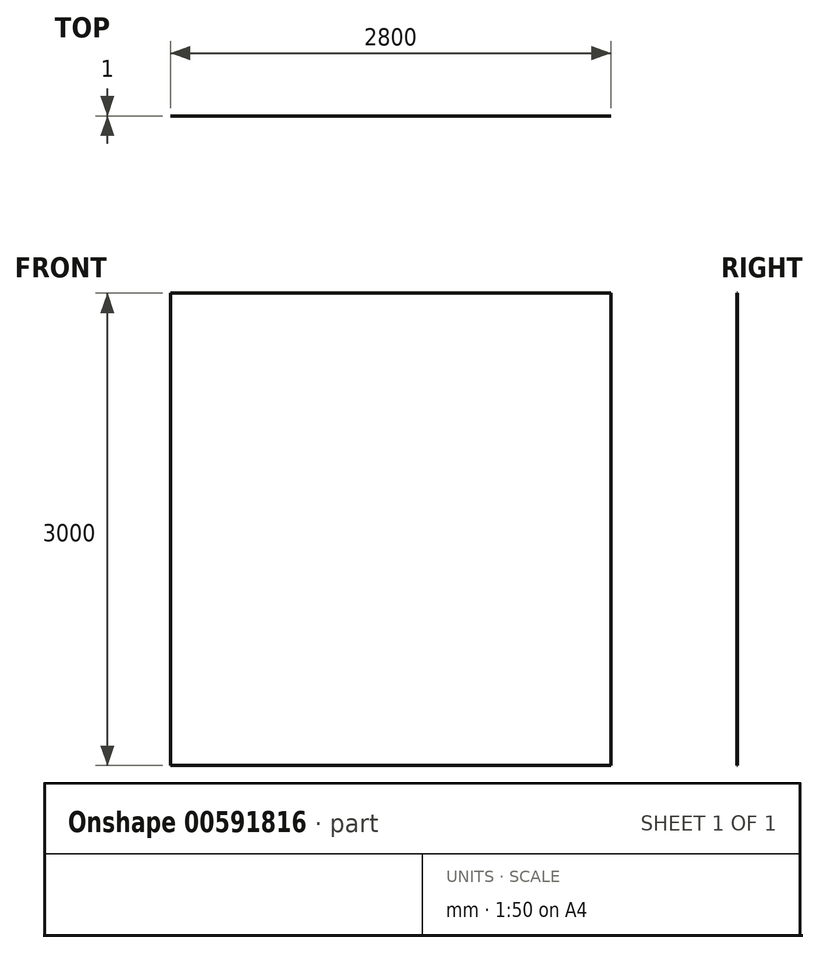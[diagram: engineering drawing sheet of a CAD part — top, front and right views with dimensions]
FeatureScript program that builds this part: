
annotation { "Feature Type Name" : "Feature", "Feature Type Description" : "" }
export const myFeature = defineFeature(function(context is Context, id is Id, definition is map)
    precondition{}
    {
        {
            var Q0;
            Q0=qCreatedBy(makeId("Front.planeOp"),FACE);
            var sketch = newSketch(context, id + "F0", { "sketchPlane" : qUnion([Q0])});
            skLineSegment(sketch, "E0.bottom", {"start": v(0, 0) * mm, "end": v(2800, 0) * mm});
            skLineSegment(sketch, "E0.top", {"start": v(0, 3000) * mm, "end": v(2800, 3000) * mm});
            skLineSegment(sketch, "E0.left", {"start": v(0, 0) * mm, "end": v(0, 3000) * mm});
            skLineSegment(sketch, "E0.right", {"start": v(2800, 0) * mm, "end": v(2800, 3000) * mm});
            skSolve(sketch);
        }
        {
            var Q0;
            Q0=makeQuery(id+"F0.imprint","IMPRINT",FACE,{"disambiguationData":[TD([[makeQuery(id+"F0.imprint","IMPRINT",EDGE,{"derivedFrom":sQuery(id+"F0.wireOp",EDGE,"E0.bottom")}),1.0]])]});
            extrude(context, id + "F1", {"entities" : qUnion([Q0]), "depth" : 1 * mm, "offsetDistance" : 25 * mm});
        }
    });
